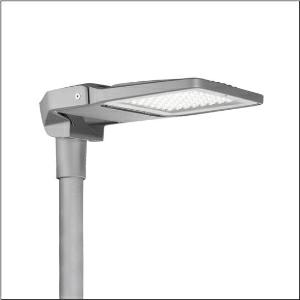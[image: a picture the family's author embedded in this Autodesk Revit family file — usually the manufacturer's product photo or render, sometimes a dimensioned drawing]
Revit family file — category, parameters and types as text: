
# Revit family: floodlight_fl_20_mini___pl52_5xa7672c1d4ac_71bc
name_source: partatom
category: Lighting Fixtures
units: mm (PartAtom-declared; Revit-internal decimal feet)

## family parameters
Cut with Voids When Loaded = No
Host = Face
Light Source = No
Part Type = Normal
Room Calculation Point = No
Round Connector Dimension = Use Diameter
Shared = No

## types (1)
- --- (1 x LED 3000K / CRI = 80 (unbekannt), 9640 lm, 3000K)
    Apparent Load = 96 VA
    CIE Flux Codes = 27 59 98 100 100
    Color Rendering = 80
    Color Temperature = 3000K
    Default Elevation = 1800 mm
    Description = Floodlight FL 20 mini, floodlight, primary light control with lens, of plastic, primary optical cover: protective disc, of toughened safety glass, transparent, light distribution: PL52, light emission: direct distribution, primary light characteristic: asymmetric, installation type: side-entry, post-top, LED, High Power LED, rated luminous flux: 9.640lm, luminous efficacy: 101lm/W, light colour: 830, colour temperature: 3000K, control gear: ECG Plus, control: flexible luminous flux parameterisation, time-dependent luminous flux control, digital communication interface, overheat protection, power reduction, electronic power reduction, with terminal, 5-pole, max. 2.5mm², mains connection: 220..240V, AC, 50/60Hz, rated input power: 96W, LED unit, of diecast aluminium, powder-coated, Siteco® metallic grey (DB 702S), corrosivity category C5 mid according to DIN EN ISO 12944, incl. 1x M20 cable gland for cable Ø 6.5..12mm, inclination adjustable: 0°, 5°, 10°, 15°, please order mast flange separately, length: 565mm, width: 335mm, height: 119mm, housing frame, of diecast aluminium, powder-coated, Siteco® metallic grey (DB 702S), mast flange adapter, of diecast aluminium, powder-coated, Siteco® metallic grey (DB 702S), DALI, protection rating (complete): IP66, insulation class (complete): insulation class II (safety insulation), certification: CE, ENEC, VDE, protection symbol: D, permissible operating ambient temperature: -40..+40°C, permissible operating ambient temperature for outdoor applications: -40..+50°C, standard: DIN EN 12944, packaging unit: 1 piece

Light Distribution: PL52
    Height = 62 mm  [stored 0.203412 ft]
    Lamp = 1 x LED 3000K / CRI >= 80 (unbekannt)
    Lamp Light Flux = 9640 lm
    Lamp count = 1
    Length = 565 mm
    Luminous efficacy = 101 lm/W
    Manufacturer = Siteco
    ModVariant = No
    Model = 5XA7672C1D4AC
    Number of Poles = 1
    OnlyDefault = Yes
    Power Factor = 1
    Product Name = Floodlight FL 20 mini | PL52
    Product group = floodlight | pylon top
    ProductGroupID = 6101
    Protection Class = Protection class II
    Protection Degree = IP 66
    RLX_Detail_Level = 1
    RLX_Emergency_Light_Flux = 0 lm
    RLX_Emergency_Type = 0
    RLX_Emergency_Type_DB = No
    RlxData = <blob elided: 101965 chars, md5=97f44709>
    Socket = socket
    Standby Power = 0 W
    System Light Flux = 9640 lm
    System Power = 96 W
    Type Comments = factory setting: luminous flux: 100 % | dim-lin: 254 | 500 mA
    Type Image = l_1005946.jpg
    URL = http://relux.com
    VarID = @adj_163633
    Voltage = 0 V
    Weight = 0.00 kg
    Width = 335 mm

note: [stored X ft] marks values corroborated as IEEE doubles in the binary element streams (Revit-internal decimal feet)

## geometry (parser evidence)
native form markers: Blend x4, Sweep x13
no freeform markers — native parametric forms only
